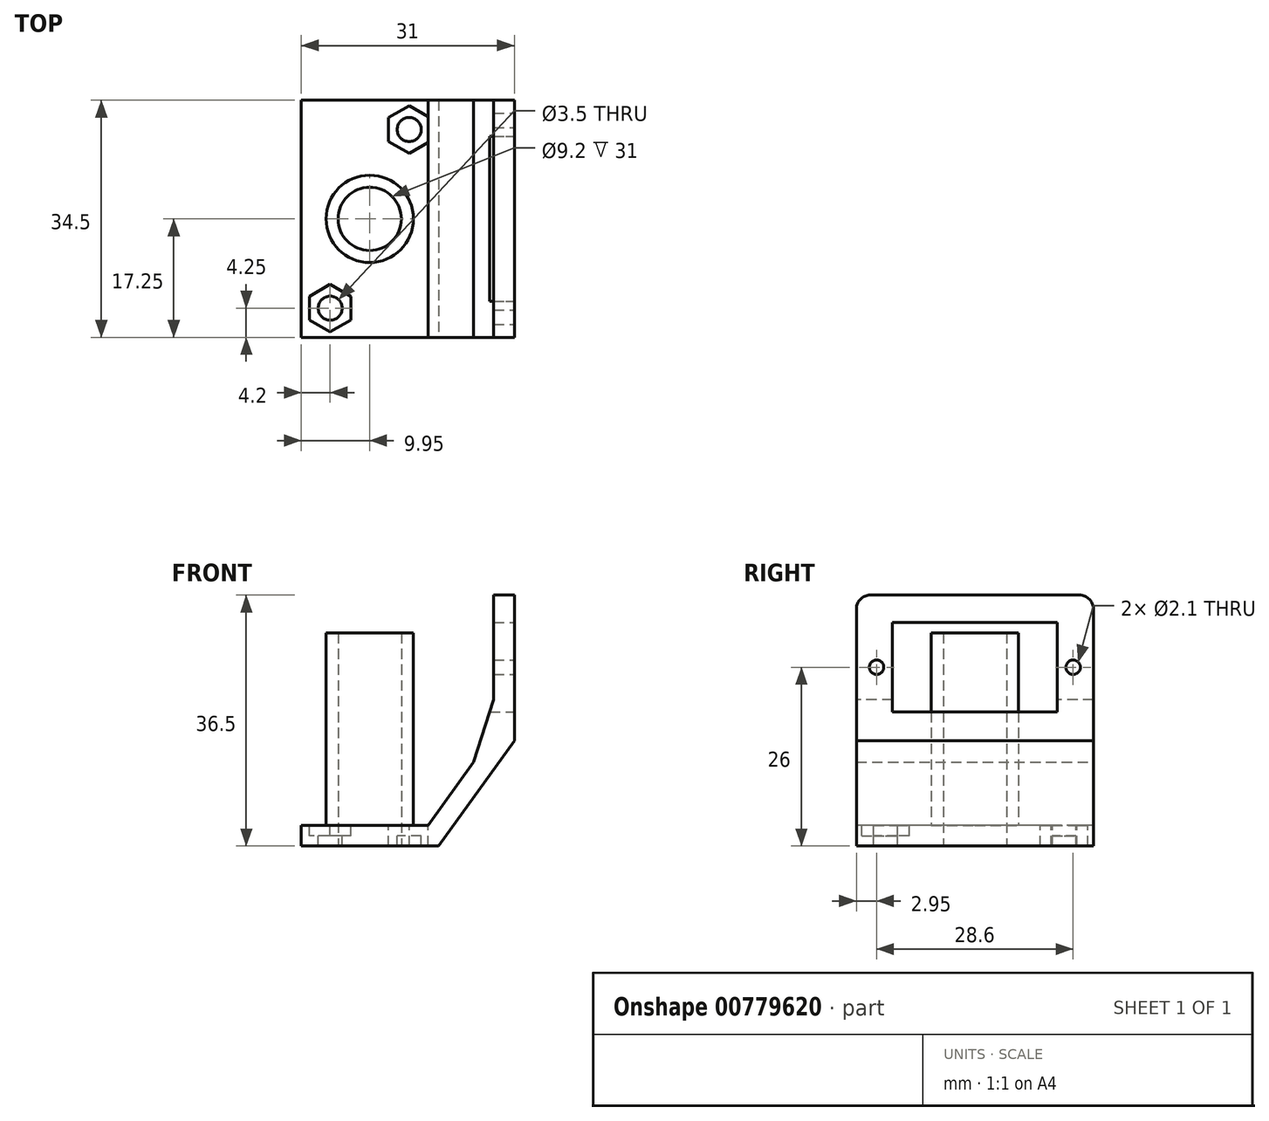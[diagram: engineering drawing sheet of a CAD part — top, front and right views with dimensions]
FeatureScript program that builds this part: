
annotation { "Feature Type Name" : "Feature", "Feature Type Description" : "" }
export const myFeature = defineFeature(function(context is Context, id is Id, definition is map)
    precondition{}
    {
        {
            var Q0;
            Q0=qCreatedBy(makeId("Top.planeOp"),FACE);
            var sketch = newSketch(context, id + "F0", { "sketchPlane" : qUnion([Q0])});
            skLineSegment(sketch, "E0.bottom", {"start": v(-15.5, 17.25) * mm, "end": v(15.5, 17.25) * mm});
            skLineSegment(sketch, "E0.top", {"start": v(-15.5, -17.25) * mm, "end": v(15.5, -17.25) * mm});
            skLineSegment(sketch, "E0.left", {"start": v(-15.5, 17.25) * mm, "end": v(-15.5, -17.25) * mm});
            skLineSegment(sketch, "E0.right", {"start": v(15.5, 17.25) * mm, "end": v(15.5, -17.25) * mm});
            skPoint(sketch, "E0.middle", {"position": v(0, 0) * mm});
            skSolve(sketch);
        }
        {
            var Q0;
            Q0 = qSketchRegion(id + "F0", true);
            extrude(context, id + "F1", {"entities" : qUnion([Q0]), "depth" : 36.5 * mm, "offsetDistance" : 25 * mm});
        }
        {
            var Q0;
            Q0=makeQuery(id+"F1.opExtrude","SWEPT_FACE",FACE,{"disambiguationData":[OSD([sQuery(id+"F0.wireOp",EDGE,"E0.top")])]});
            var sketch = newSketch(context, id + "F2", { "sketchPlane" : qUnion([Q0])});
            skLineSegment(sketch, "E1", {"start": v(-15.5, 0) * mm, "end": v(4.5, 0) * mm});
            skLineSegment(sketch, "E2", {"start": v(4.5, 0) * mm, "end": v(15.5, 15.3) * mm});
            skLineSegment(sketch, "E3", {"start": v(15.5, 15.3) * mm, "end": v(15.5, 36.5) * mm});
            skLineSegment(sketch, "E4.0", {"start": v(12.5, 16.27) * mm, "end": v(12.5, 36.5) * mm});
            skLineSegment(sketch, "E4.1", {"start": v(2.96, 3) * mm, "end": v(12.5, 16.27) * mm});
            skLineSegment(sketch, "E4.2", {"start": v(-15.5, 3) * mm, "end": v(2.96, 3) * mm});
            skLineSegment(sketch, "E5", {"start": v(15.5, 36.5) * mm, "end": v(12.5, 36.5) * mm});
            skLineSegment(sketch, "E6", {"start": v(-15.5, 3) * mm, "end": v(-15.5, 0) * mm});
            skSolve(sketch);
        }
        {
            var Q0;
            {var subQ5=sQuery(id+"F2.wireOp",EDGE,"E4.0");Q0=makeQuery(id+"F2.imprint","IMPRINT",FACE,{"disambiguationData":[TD([[makeQuery(id+"F2.imprint","IMPRINT",EDGE,{"derivedFrom":subQ5}),1.0]])]});}
            var Q1;
            {var subQ0=sQuery(id+"F2.wireOp",EDGE,"E2");Q1=makeQuery(id+"F2.imprint","IMPRINT",FACE,{"disambiguationData":[TD([[makeQuery(id+"F2.imprint","IMPRINT",EDGE,{"derivedFrom":subQ0}),-1.0]])]});}
            var Q2;
            Q2=makeQuery(id+"F1.opExtrude","SWEPT_FACE",FACE,{"disambiguationData":[OSD([sQuery(id+"F0.wireOp",EDGE,"E0.bottom")])]});
            extrude(context, id + "F3", {"entities" : qUnion([Q0, Q1]), "operationType" : NewBodyOperationType.REMOVE, "endBound" : BoundingType.UP_TO_SURFACE, "oppositeDirection" : true, "depth" : 25 * mm, "endBoundEntityFace" : qUnion([Q2]), "offsetDistance" : 25 * mm});
        }
        {
            var Q0;
            Q0=makeQuery(id+"F3.boolean.opBoolean","COPY",FACE,{"derivedFrom":makeQuery(id+"F3.opExtrude","SWEPT_FACE",FACE,{"disambiguationData":[OSD([sQuery(id+"F2.wireOp",EDGE,"E4.2")])]})});
            var sketch = newSketch(context, id + "F4", { "sketchPlane" : qUnion([Q0])});
            skCircle(sketch, "E7", {"center": v(-11.3, -13) * mm, "radius": 1.75 * mm});
            skCircle(sketch, "E8.MirrorC", {"center": v(0.2, 13) * mm, "radius": 1.75 * mm});
            skLineSegment(sketch, "E9", {"start": v(-1.55, 13) * mm, "end": v(-1.55, -13) * mm, "construction": true});
            skCircle(sketch, "E10.cCircle", {"center": v(-11.3, -13) * mm, "radius": 3 * mm, "construction": true});
            skLineSegment(sketch, "E10.0", {"start": v(-14.3, -14.73) * mm, "end": v(-14.3, -11.27) * mm});
            skLineSegment(sketch, "E10.1", {"start": v(-14.3, -11.27) * mm, "end": v(-11.3, -9.54) * mm});
            skLineSegment(sketch, "E10.2", {"start": v(-11.3, -9.54) * mm, "end": v(-8.3, -11.27) * mm});
            skLineSegment(sketch, "E10.3", {"start": v(-8.3, -11.27) * mm, "end": v(-8.3, -14.73) * mm});
            skLineSegment(sketch, "E10.4", {"start": v(-8.3, -14.73) * mm, "end": v(-11.3, -16.46) * mm});
            skLineSegment(sketch, "E10.5", {"start": v(-11.3, -16.46) * mm, "end": v(-14.3, -14.73) * mm});
            skPoint(sketch, "E10.0.midPoint", {"position": v(-14.3, -13) * mm});
            skCircle(sketch, "E11.cCircle", {"center": v(0.2, 13) * mm, "radius": 3 * mm, "construction": true});
            skLineSegment(sketch, "E11.0", {"start": v(-2.8, 14.73) * mm, "end": v(0.2, 16.46) * mm});
            skLineSegment(sketch, "E11.1", {"start": v(0.2, 16.46) * mm, "end": v(3.2, 14.73) * mm});
            skLineSegment(sketch, "E11.2", {"start": v(3.2, 14.73) * mm, "end": v(3.2, 11.27) * mm});
            skLineSegment(sketch, "E11.3", {"start": v(3.2, 11.27) * mm, "end": v(0.2, 9.54) * mm});
            skLineSegment(sketch, "E11.4", {"start": v(0.2, 9.54) * mm, "end": v(-2.8, 11.27) * mm});
            skLineSegment(sketch, "E11.5", {"start": v(-2.8, 11.27) * mm, "end": v(-2.8, 14.73) * mm});
            skPoint(sketch, "E11.0.midPoint", {"position": v(-1.3, 15.6) * mm});
            skLineSegment(sketch, "E12", {"start": v(0.2, 16.46) * mm, "end": v(0.2, 17.25) * mm, "construction": true});
            skLineSegment(sketch, "E13", {"start": v(-11.3, -16.46) * mm, "end": v(-11.3, -17.25) * mm, "construction": true});
            skLineSegment(sketch, "E14", {"start": v(-9.55, -13) * mm, "end": v(-9.55, 11.84) * mm, "construction": true});
            skSolve(sketch);
        }
        {
            var Q0;
            Q0=makeQuery(id+"F3.boolean.opBoolean","COPY",FACE,{"derivedFrom":makeQuery(id+"F3.opExtrude","SWEPT_FACE",FACE,{"disambiguationData":[OSD([sQuery(id+"F2.wireOp",EDGE,"E4.2")])]})});
            var sketch = newSketch(context, id + "F5", { "sketchPlane" : qUnion([Q0])});
            skCircle(sketch, "E15.0", {"center": v(-5.55, 0) * mm, "radius": 4.6 * mm});
            skCircle(sketch, "E16.0", {"center": v(-5.55, 0) * mm, "radius": 6.35 * mm});
            skSolve(sketch);
        }
        {
            var Q0;
            Q0 = qSketchRegion(id + "F5", true);
            extrude(context, id + "F6", {"entities" : qUnion([Q0]), "operationType" : NewBodyOperationType.ADD, "depth" : 28 * mm, "offsetDistance" : 25 * mm});
        }
        {
            var Q0;
            Q0=makeQuery(id+"F1.opExtrude","SWEPT_FACE",FACE,{"disambiguationData":[OSD([sQuery(id+"F0.wireOp",EDGE,"E0.right")])]});
            var sketch = newSketch(context, id + "F7", { "sketchPlane" : qUnion([Q0])});
            skLineSegment(sketch, "E17.bottom", {"start": v(0.3, 32.5) * mm, "end": v(-12, 32.5) * mm});
            skLineSegment(sketch, "E17.top", {"start": v(0.3, 19.5) * mm, "end": v(-12, 19.5) * mm});
            skLineSegment(sketch, "E17.left", {"start": v(0.3, 32.5) * mm, "end": v(0.3, 19.5) * mm});
            skLineSegment(sketch, "E17.right", {"start": v(-12, 32.5) * mm, "end": v(-12, 19.5) * mm});
            skLineSegment(sketch, "E18.bottom", {"start": v(-0.3, 32.5) * mm, "end": v(12, 32.5) * mm});
            skLineSegment(sketch, "E18.top", {"start": v(-0.3, 19.5) * mm, "end": v(12, 19.5) * mm});
            skLineSegment(sketch, "E18.left", {"start": v(-0.3, 32.5) * mm, "end": v(-0.3, 19.5) * mm});
            skLineSegment(sketch, "E18.right", {"start": v(12, 32.5) * mm, "end": v(12, 19.5) * mm});
            skLineSegment(sketch, "E19", {"start": v(-12, 32.5) * mm, "end": v(-17.25, 32.5) * mm, "construction": true});
            skLineSegment(sketch, "E20", {"start": v(12, 32.5) * mm, "end": v(17.25, 32.5) * mm, "construction": true});
            skPoint(sketch, "E21.0", {"position": v(0, 36.5) * mm});
            skPoint(sketch, "E22.0", {"position": v(0, 0) * mm});
            skCircle(sketch, "E23", {"center": v(-14.3, 26) * mm, "radius": 1.05 * mm});
            skPoint(sketch, "E23.centerSnap0", {"position": v(-12, 26) * mm});
            skCircle(sketch, "E24", {"center": v(14.3, 26) * mm, "radius": 1.05 * mm});
            skLineSegment(sketch, "E25", {"start": v(-14.3, 26) * mm, "end": v(-17.25, 26) * mm, "construction": true});
            skLineSegment(sketch, "E26", {"start": v(17.25, 26) * mm, "end": v(14.3, 26) * mm, "construction": true});
            skSolve(sketch);
        }
        {
            var Q0;
            {var subQ0=sQuery(id+"F7.wireOp",EDGE,"E17.left");Q0=makeQuery(id+"F7.imprint","IMPRINT",FACE,{"disambiguationData":[TD([[makeQuery(id+"F7.imprint","IMPRINT",EDGE,{"derivedFrom":subQ0}),1.0]])]});}
            var Q1;
            Q1=makeQuery(id+"F7.imprint","IMPRINT",FACE,{"disambiguationData":[TD([[makeQuery(id+"F7.imprint","IMPRINT",EDGE,{"derivedFrom":sQuery(id+"F7.wireOp",EDGE,"E17.bottom")}),1.0]])]});
            var Q2;
            Q2=makeQuery(id+"F7.imprint","IMPRINT",FACE,{"disambiguationData":[TD([[makeQuery(id+"F7.imprint","IMPRINT",EDGE,{"derivedFrom":sQuery(id+"F7.wireOp",EDGE,"E23")}),1.0]])]});
            var Q3;
            Q3=makeQuery(id+"F7.imprint","IMPRINT",FACE,{"disambiguationData":[TD([[makeQuery(id+"F7.imprint","IMPRINT",EDGE,{"derivedFrom":sQuery(id+"F7.wireOp",EDGE,"E24")}),1.0]])]});
            var Q4;
            Q4=makeQuery(id+"F3.boolean.opBoolean","COPY",FACE,{"derivedFrom":makeQuery(id+"F3.opExtrude","SWEPT_FACE",FACE,{"disambiguationData":[OSD([sQuery(id+"F2.wireOp",EDGE,"E4.0")])]})});
            extrude(context, id + "F8", {"entities" : qUnion([Q0, Q1, Q2, Q3]), "operationType" : NewBodyOperationType.REMOVE, "endBound" : BoundingType.UP_TO_SURFACE, "oppositeDirection" : true, "depth" : 25 * mm, "endBoundEntityFace" : qUnion([Q4]), "offsetDistance" : 25 * mm});
        }
        {
            var Q0;
            Q0=makeQuery(id+"F4.imprint","IMPRINT",FACE,{"disambiguationData":[TD([[makeQuery(id+"F4.imprint","IMPRINT",EDGE,{"derivedFrom":sQuery(id+"F4.wireOp",EDGE,"E7")}),1.0]])]});
            var Q1;
            Q1=makeQuery(id+"F4.imprint","IMPRINT",FACE,{"disambiguationData":[TD([[makeQuery(id+"F4.imprint","IMPRINT",EDGE,{"derivedFrom":sQuery(id+"F4.wireOp",EDGE,"4dlwz30R-9sRD-0B62-ILum-S8ZCcvPe33iH")}),1.0]])]});
            var Q2;
            Q2=makeQuery(id+"F4.imprint","IMPRINT",FACE,{"disambiguationData":[TD([[makeQuery(id+"F4.imprint","IMPRINT",EDGE,{"derivedFrom":sQuery(id+"F4.wireOp",EDGE,"E8.MirrorC")}),-1.0]])]});
            var Q3;
            Q3=makeQuery(id+"F4.imprint","IMPRINT",FACE,{"disambiguationData":[TD([[makeQuery(id+"F4.imprint","IMPRINT",EDGE,{"derivedFrom":sQuery(id+"F4.wireOp",EDGE,"3b07cae0-9ddf-4b37-a280-d5cf03c90af10.MirrorC")}),-1.0]])]});
            var Q4;
            Q4=makeQuery(id+"F1.opExtrude","CAP_FACE",FACE,{"disambiguationData":[OSD([sQuery(id+"F0.wireOp",EDGE,"E0.bottom"),sQuery(id+"F0.wireOp",EDGE,"E0.top"),sQuery(id+"F0.wireOp",EDGE,"E0.left"),sQuery(id+"F0.wireOp",EDGE,"E0.right"),sQuery(id+"F0.wireOp",EDGE,"lM0Awef6-8gsq-uQGH-dHPc-xlV5KpjtTDTr")])],"isStart":true});
            extrude(context, id + "F9", {"entities" : qUnion([Q0, Q1, Q2, Q3]), "operationType" : NewBodyOperationType.REMOVE, "endBound" : BoundingType.UP_TO_SURFACE, "oppositeDirection" : true, "depth" : 25 * mm, "endBoundEntityFace" : qUnion([Q4]), "offsetDistance" : 25 * mm});
        }
        {
            var Q0;
            Q0=makeQuery(id+"F4.imprint","IMPRINT",FACE,{"disambiguationData":[TD([[makeQuery(id+"F4.imprint","IMPRINT",EDGE,{"derivedFrom":sQuery(id+"F4.wireOp",EDGE,"E7")}),-1.0]])]});
            var Q1;
            Q1=makeQuery(id+"F4.imprint","IMPRINT",FACE,{"disambiguationData":[TD([[makeQuery(id+"F4.imprint","IMPRINT",EDGE,{"derivedFrom":sQuery(id+"F4.wireOp",EDGE,"4dlwz30R-9sRD-0B62-ILum-S8ZCcvPe33iH")}),-1.0]])]});
            var Q2;
            Q2=makeQuery(id+"F4.imprint","IMPRINT",FACE,{"disambiguationData":[TD([[makeQuery(id+"F4.imprint","IMPRINT",EDGE,{"derivedFrom":sQuery(id+"F4.wireOp",EDGE,"3b07cae0-9ddf-4b37-a280-d5cf03c90af10.MirrorC")}),1.0]])]});
            var Q3;
            Q3=makeQuery(id+"F4.imprint","IMPRINT",FACE,{"disambiguationData":[TD([[makeQuery(id+"F4.imprint","IMPRINT",EDGE,{"derivedFrom":sQuery(id+"F4.wireOp",EDGE,"E8.MirrorC")}),1.0]])]});
            extrude(context, id + "F10", {"entities" : qUnion([Q0, Q1, Q2, Q3]), "operationType" : NewBodyOperationType.REMOVE, "oppositeDirection" : true, "depth" : 1.5 * mm, "offsetDistance" : 25 * mm});
        }
        {
            var Q0;
            Q0=makeQuery(id+"F5.imprint","IMPRINT",FACE,{"disambiguationData":[TD([[makeQuery(id+"F5.imprint","IMPRINT",EDGE,{"derivedFrom":sQuery(id+"F5.wireOp",EDGE,"E15.0")}),1.0]])]});
            var Q1;
            Q1=makeQuery(id+"F1.opExtrude","CAP_FACE",FACE,{"disambiguationData":[OSD([sQuery(id+"F0.wireOp",EDGE,"E0.bottom"),sQuery(id+"F0.wireOp",EDGE,"E0.top"),sQuery(id+"F0.wireOp",EDGE,"E0.left"),sQuery(id+"F0.wireOp",EDGE,"E0.right")])],"isStart":true});
            extrude(context, id + "F11", {"entities" : qUnion([Q0]), "operationType" : NewBodyOperationType.REMOVE, "endBound" : BoundingType.UP_TO_SURFACE, "oppositeDirection" : true, "depth" : 25 * mm, "endBoundEntityFace" : qUnion([Q1]), "offsetDistance" : 25 * mm});
        }
        {
            var Q0;
            Q0=makeQuery(id+"F1.opExtrude","CAP_EDGE",EDGE,{"disambiguationData":[OSD([sQuery(id+"F0.wireOp",EDGE,"E0.top")])],"isStart":false});
            var Q1;
            Q1=makeQuery(id+"F1.opExtrude","CAP_EDGE",EDGE,{"disambiguationData":[OSD([sQuery(id+"F0.wireOp",EDGE,"E0.bottom")])],"isStart":false});
            fillet(context, id + "F12", {"entities" : qUnion([Q0, Q1]), "tangentPropagation" : true, "radius" : 2 * mm, "defaultsChanged" : true, "vertexSettings" : [], "allowEdgeOverflow" : false});
        }
        {
            var Q0;
            Q0=makeQuery(id+"F3.boolean.opBoolean","COPY",EDGE,{"derivedFrom":makeQuery(id+"F3.opExtrude","SWEPT_EDGE",EDGE,{"disambiguationData":[OSD([sQuery(id+"F0.wireOp",EDGE,"E0.top"),sQuery(id+"F0.wireOp",EDGE,"E0.right"),sQuery(id+"F2.wireOp",EDGE,"E2"),sQuery(id+"F2.wireOp",EDGE,"E3")])]})});
            var Q1;
            Q1=makeQuery(id+"F3.boolean.opBoolean","COPY",EDGE,{"derivedFrom":makeQuery(id+"F3.opExtrude","SWEPT_EDGE",EDGE,{"disambiguationData":[OSD([sQuery(id+"F2.wireOp",EDGE,"E4.0"),sQuery(id+"F2.wireOp",EDGE,"E4.1")])]})});
            chamfer(context, id + "F13", {"entities" : qUnion([Q0, Q1]), "width" : 5 * mm, "tangentPropagation" : true});
        }
    });
